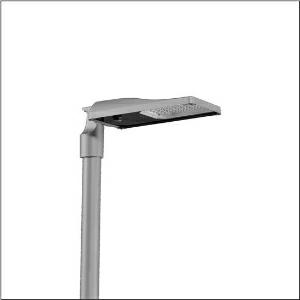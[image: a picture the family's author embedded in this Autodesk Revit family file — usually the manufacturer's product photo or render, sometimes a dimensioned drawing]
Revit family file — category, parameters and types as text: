
# Revit family: streetlight_sl_31_mini___st1_0a_5xh6d3ar08ga_0704
name_source: partatom
category: Lighting Fixtures
units: mm (PartAtom-declared; Revit-internal decimal feet)

## family parameters
Cut with Voids When Loaded = No
Host = Face
Light Source = No
Part Type = Normal
Room Calculation Point = No
Round Connector Dimension = Use Diameter
Shared = No

## types (1)
- --- (1 x LED, 5880 lm, 39.3 W, 3000K)
    Apparent Load = 39 VA
    CIE Flux Codes = 37 72 97 100 100
    Color Rendering = 70
    Color Temperature = 3000K
    Default Elevation = 1800 mm
    Description = Streetlight SL 31 mini D4i mast luminaire for post-top, side-entry; light control with lens of PMMA; light distribution: ST1.0a, direct asymmetric distribution, for standard-compliant lighting for roads and squares; LED: luminous flux: 5.880lm, light colour: 730, colour temperature: 3000K; luminous efficacy: 149,6lm/W; control: pre-setting: logarithmic dimming characteristic, flexible luminous flux parameterisation, time-dependent luminous flux control, constant luminous flux control, power reduction, intelligent temperature release in ECG and LED module, overheat protection; luminaire housing, of diecast aluminium, Siteco® metallic grey (DB 702S), corrosivity category C5 high according to DIN EN ISO 12944; cover of toughened safety glass, transparent, opened without tools; mast flange of diecast aluminium, Siteco® metallic grey (DB 702S), spigot size: 76/60mm, mast flange included unmounted; with cable H07RN-F 2x 1.5mm², cable length: 6,5m, connection cable pre-assembled; mains connection: 220..240V, AC, 50/60Hz; power consumption (at start of service life): 39,3W / (at end of service life): 40,7W / (with reduced operation 50%): 18,1W; protection rating (complete): IP66; insulation class (complete): insulation class II (safety insulation); impact resistance: IK09; certification: CE, ENEC, ENEC+, VDE, UKCA, ZD4i; permissible operating ambient temperature for outdoor applications: -40..+50°C; packaging unit: 1 piece

Light Distribution: ST1.0a
    Height = 76 mm
    Lamp = 1 x LED
    Lamp Light Flux = 5880 lm
    Lamp Power = 39.3 W
    Lamp count = 1
    Length = 547 mm
    Luminous efficacy = 150 lm/W
    Manufacturer = Siteco
    ModVariant = No
    Model = 5XH6D3AR08GA
    Number of Poles = 1
    OnlyDefault = Yes
    Power Factor = 1
    Product Name = Streetlight SL 31 mini | ST1.0a
    Product group = mast luminaire | pylon top
    ProductGroupID = 6100
    Protection Class = Protection class II
    Protection Degree = IP 66
    RLX_Detail_Level = 1
    RLX_Emergency_Light_Flux = 0 lm
    RLX_Emergency_Type = 0
    RLX_Emergency_Type_DB = No
    RlxData = <blob elided: 39677 chars, md5=e91f7c21>
    Socket = socket
    Standby Power = 0 W
    System Light Flux = 5880 lm
    System Power = 39 W
    Type Comments = factory setting: luminous flux: 100 % | dim-lin: 254 | 798 mA
    Type Image = l_1300328.jpg
    URL = http://relux.com
    VarID = @adj_054036
    Voltage = 0 V
    Weight = 0.00 kg
    Width = 265 mm

## geometry (parser evidence)
native form markers: Blend x4, Sweep x10
no freeform markers — native parametric forms only
